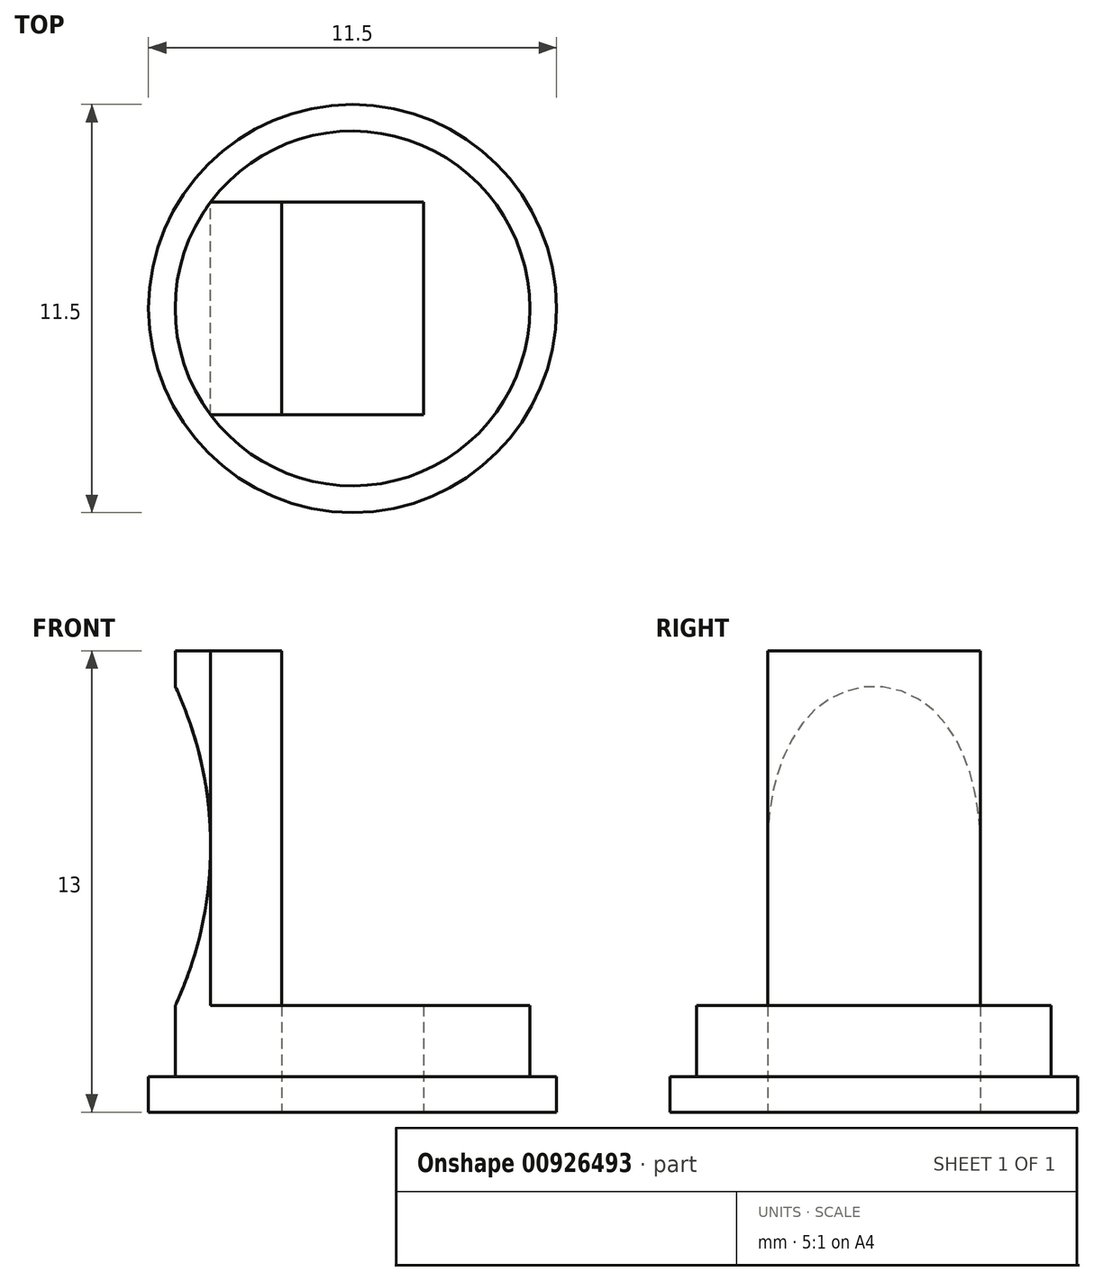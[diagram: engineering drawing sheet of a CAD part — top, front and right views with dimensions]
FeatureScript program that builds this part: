
annotation { "Feature Type Name" : "Feature", "Feature Type Description" : "" }
export const myFeature = defineFeature(function(context is Context, id is Id, definition is map)
    precondition{}
    {
        {
            var Q0;
            Q0=qCreatedBy(makeId("Top.planeOp"),FACE);
            var sketch = newSketch(context, id + "F0", { "sketchPlane" : qUnion([Q0])});
            skLineSegment(sketch, "E0.bottom", {"start": v(0, 0) * mm, "end": v(-4, 0) * mm});
            skLineSegment(sketch, "E0.top", {"start": v(0, -6) * mm, "end": v(-4, -6) * mm});
            skLineSegment(sketch, "E0.left", {"start": v(0, 0) * mm, "end": v(0, -6) * mm});
            skLineSegment(sketch, "E0.right", {"start": v(-4, 0) * mm, "end": v(-4, -6) * mm});
            skLineSegment(sketch, "E1", {"start": v(-4, -3) * mm, "end": v(0, -3) * mm, "construction": true});
            skPoint(sketch, "E2", {"position": v(-2, -3) * mm});
            skCircle(sketch, "E3", {"center": v(-2, -3) * mm, "radius": 5 * mm});
            skSolve(sketch);
        }
        {
            var Q0;
            Q0 = qSketchRegion(id + "F0", true);
            extrude(context, id + "F1", {"entities" : qUnion([Q0]), "depth" : 2 * mm, "offsetDistance" : 25 * mm});
        }
        {
            var Q0;
            Q0=makeQuery(id+"F1.opExtrude","CAP_FACE",FACE,{"disambiguationData":[OSD([sQuery(id+"F0.wireOp",EDGE,"E0.bottom"),sQuery(id+"F0.wireOp",EDGE,"E0.top"),sQuery(id+"F0.wireOp",EDGE,"E0.left"),sQuery(id+"F0.wireOp",EDGE,"E0.right"),sQuery(id+"F0.wireOp",EDGE,"E3")])],"isStart":true});
            var sketch = newSketch(context, id + "F2", { "sketchPlane" : qUnion([Q0])});
            skLineSegment(sketch, "E4.0", {"start": v(-4, 0) * mm, "end": v(-4, 6) * mm});
            skLineSegment(sketch, "E4.1", {"start": v(0, 0) * mm, "end": v(-4, 0) * mm});
            skLineSegment(sketch, "E4.2", {"start": v(0, 0) * mm, "end": v(0, 6) * mm});
            skLineSegment(sketch, "E4.3", {"start": v(0, 6) * mm, "end": v(-4, 6) * mm});
            skCircle(sketch, "E5", {"center": v(-2, 3) * mm, "radius": 5.75 * mm});
            skSolve(sketch);
        }
        {
            var Q0;
            Q0 = qSketchRegion(id + "F2", true);
            extrude(context, id + "F3", {"entities" : qUnion([Q0]), "operationType" : NewBodyOperationType.ADD, "depth" : 1 * mm, "offsetDistance" : 25 * mm});
        }
        {
            var Q0;
            Q0=makeQuery(id+"F1.opExtrude","CAP_FACE",FACE,{"disambiguationData":[OSD([sQuery(id+"F0.wireOp",EDGE,"E0.bottom"),sQuery(id+"F0.wireOp",EDGE,"E0.top"),sQuery(id+"F0.wireOp",EDGE,"E0.left"),sQuery(id+"F0.wireOp",EDGE,"E0.right"),sQuery(id+"F0.wireOp",EDGE,"E3")])],"isStart":false});
            var sketch = newSketch(context, id + "F4", { "sketchPlane" : qUnion([Q0])});
            skLineSegment(sketch, "E6.0", {"start": v(-4, 0) * mm, "end": v(-4, -6) * mm});
            skLineSegment(sketch, "E7", {"start": v(-4, 0) * mm, "end": v(-6, 0) * mm});
            skLineSegment(sketch, "E8", {"start": v(-4, -6) * mm, "end": v(-6, -6) * mm});
            skArc(sketch, "E9.0", {"start": v(-6, 0) * mm, "mid": v(-7, -3) * mm, "end": v(-6, -6) * mm});
            skSolve(sketch);
        }
        {
            var Q0;
            Q0 = qSketchRegion(id + "F4", true);
            extrude(context, id + "F5", {"entities" : qUnion([Q0]), "operationType" : NewBodyOperationType.ADD, "depth" : 10 * mm, "offsetDistance" : 25 * mm});
        }
        {
            var Q0;
            Q0=makeQuery(id+"F5.opExtrude","SWEPT_FACE",FACE,{"disambiguationData":[OSD([sQuery(id+"F4.wireOp",EDGE,"E7")])]});
            var sketch = newSketch(context, id + "F6", { "sketchPlane" : qUnion([Q0])});
            skPoint(sketch, "E10.0", {"position": v(7, 12) * mm});
            skLineSegment(sketch, "E11", {"start": v(7, 12) * mm, "end": v(7, 2) * mm, "construction": true});
            skArc(sketch, "E12", {"start": v(7, 11) * mm, "mid": v(6, 6.5) * mm, "end": v(7, 2) * mm});
            skLineSegment(sketch, "E13", {"start": v(7, 2) * mm, "end": v(7, 11) * mm});
            skSolve(sketch);
        }
        {
            var Q0;
            Q0 = qSketchRegion(id + "F6", true);
            extrude(context, id + "F7", {"entities" : qUnion([Q0]), "operationType" : NewBodyOperationType.REMOVE, "endBound" : BoundingType.THROUGH_ALL, "oppositeDirection" : true, "depth" : 25 * mm, "offsetDistance" : 25 * mm});
        }
    });
